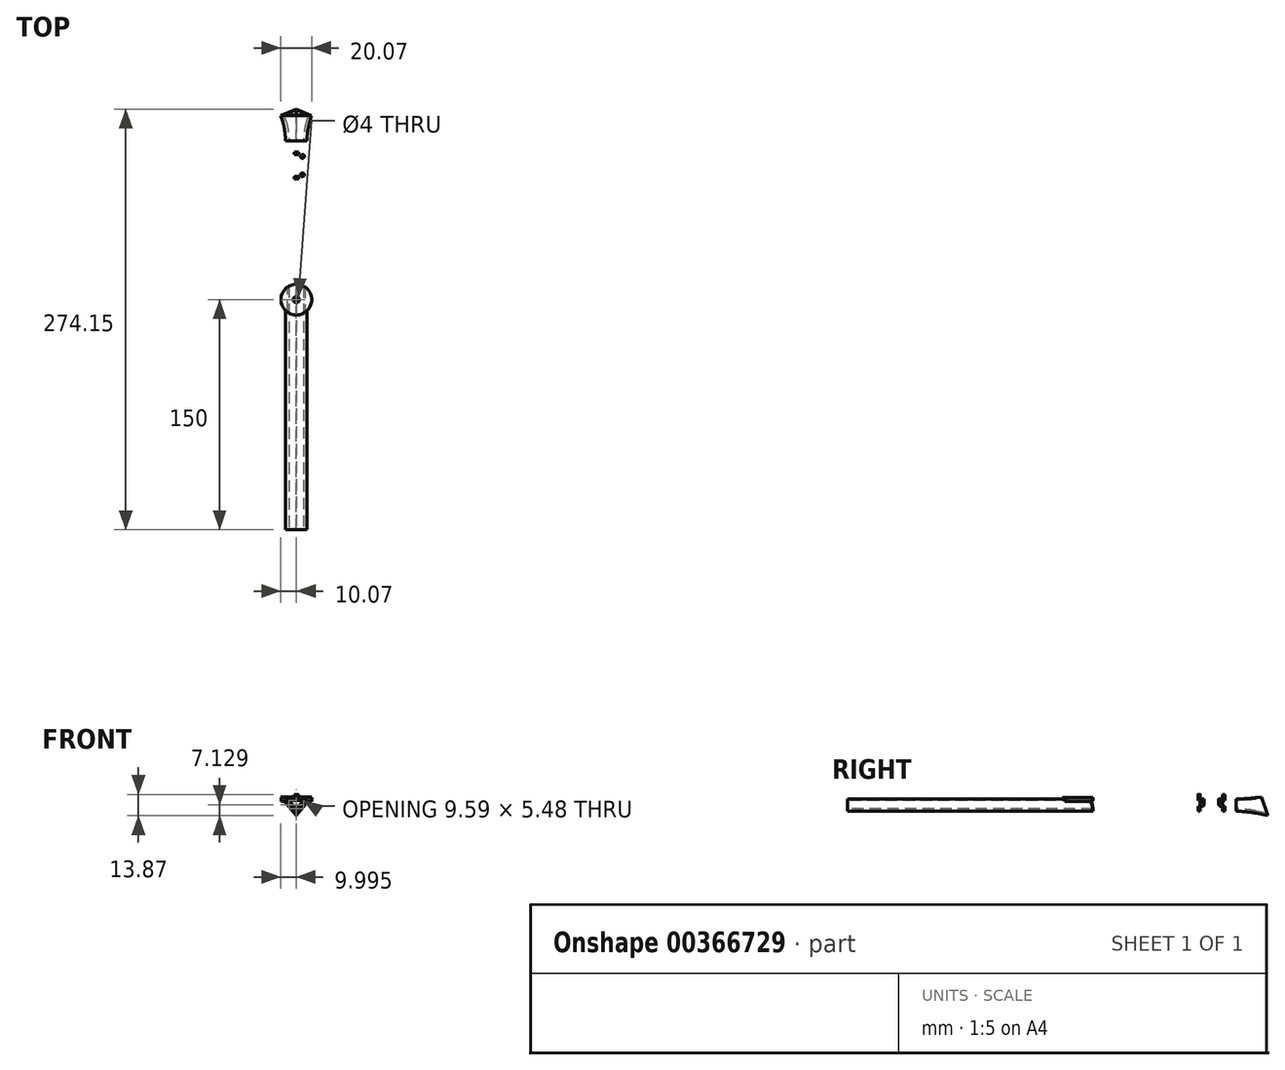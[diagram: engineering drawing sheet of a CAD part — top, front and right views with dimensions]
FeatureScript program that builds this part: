
annotation { "Feature Type Name" : "Feature", "Feature Type Description" : "" }
export const myFeature = defineFeature(function(context is Context, id is Id, definition is map)
    precondition{}
    {
        {
            var Q0;
            Q0=qCreatedBy(makeId("Front.planeOp"),FACE);
            var sketch = newSketch(context, id + "F0", { "sketchPlane" : qUnion([Q0])});
            skLineSegment(sketch, "E0", {"start": v(-7.1, 0) * mm, "end": v(6.9, 0) * mm});
            skLineSegment(sketch, "E1", {"start": v(6.9, 0) * mm, "end": v(0, -8) * mm});
            skLineSegment(sketch, "E2", {"start": v(0, -8) * mm, "end": v(-7.1, 0) * mm});
            skSolve(sketch);
        }
        {
            var Q0;
            Q0=makeQuery(id+"F0.imprint","IMPRINT",FACE,{"disambiguationData":[TD([[makeQuery(id+"F0.imprint","IMPRINT",EDGE,{"derivedFrom":sQuery(id+"F0.wireOp",EDGE,"E0")}),-1.0]])]});
            extrude(context, id + "F1", {"entities" : qUnion([Q0]), "depth" : 150 * mm});
        }
        {
            var Q0;
            Q0=makeQuery(id+"F1.opExtrude","CAP_FACE",FACE,{"disambiguationData":[OSD([sQuery(id+"F0.wireOp",EDGE,"E0"),sQuery(id+"F0.wireOp",EDGE,"E1"),sQuery(id+"F0.wireOp",EDGE,"E2")])],"isStart":true});
            extrude(context, id + "F2", {"entities" : qUnion([Q0]), "operationType" : NewBodyOperationType.ADD, "depth" : 110 * mm});
        }
        {
            var Q0;
            {var subQ0=sQuery(id+"F0.wireOp",EDGE,"E0");Q0=makeQuery(id+"F2.boolean.opBoolean","MERGE",FACE,{"derivedFrom":[makeQuery(id+"F1.opExtrude","SWEPT_FACE",FACE,{"disambiguationData":[OSD([subQ0])]}),makeQuery(id+"F2.opExtrude","SWEPT_FACE",FACE,{"disambiguationData":[OSD([subQ0])]})]});}
            var sketch = newSketch(context, id + "F3", { "sketchPlane" : qUnion([Q0])});
            skCircle(sketch, "E3", {"center": v(0, 0) * mm, "radius": 10 * mm});
            skCircle(sketch, "E4", {"center": v(0, 0) * mm, "radius": 2 * mm});
            skSolve(sketch);
        }
        {
            var Q0;
            {var subQ0=sQuery(id+"F3.wireOp",EDGE,"E3");var subQ1=sQuery(id+"F0.wireOp",EDGE,"E2");var subQ2=sQuery(id+"F0.wireOp",EDGE,"E0");var subQ3=makeQuery(id+"F2.boolean.opBoolean","MERGE",EDGE,{"derivedFrom":[makeQuery(id+"F1.opExtrude","SWEPT_EDGE",EDGE,{"disambiguationData":[OSD([subQ2,subQ1])]}),makeQuery(id+"F2.opExtrude","SWEPT_EDGE",EDGE,{"disambiguationData":[OSD([subQ2,subQ1])]})]});var subQ4=makeQuery(id+"F3.imprint","INTERSECT",VERTEX,{"disambiguationData":[OD(0.0)],"derivedFrom":[subQ3,subQ0]});Q0=makeQuery(id+"F3.imprint","IMPRINT",FACE,{"disambiguationData":[TD([[makeQuery(id+"F3.imprint","IMPRINT",EDGE,{"disambiguationData":[TD([[subQ4,1.0]])],"derivedFrom":subQ0}),1.0]])]});}
            var Q1;
            {var subQ0=sQuery(id+"F3.wireOp",EDGE,"E3");var subQ1=sQuery(id+"F0.wireOp",EDGE,"E2");var subQ2=sQuery(id+"F0.wireOp",EDGE,"E0");var subQ3=makeQuery(id+"F2.boolean.opBoolean","MERGE",EDGE,{"derivedFrom":[makeQuery(id+"F1.opExtrude","SWEPT_EDGE",EDGE,{"disambiguationData":[OSD([subQ2,subQ1])]}),makeQuery(id+"F2.opExtrude","SWEPT_EDGE",EDGE,{"disambiguationData":[OSD([subQ2,subQ1])]})]});var subQ4=makeQuery(id+"F3.imprint","INTERSECT",VERTEX,{"disambiguationData":[OD(0.0)],"derivedFrom":[subQ3,subQ0]});Q1=makeQuery(id+"F3.imprint","IMPRINT",FACE,{"disambiguationData":[TD([[makeQuery(id+"F3.imprint","IMPRINT",EDGE,{"disambiguationData":[TD([[subQ4,-1.0]])],"derivedFrom":subQ0}),1.0]])]});}
            var Q2;
            {var subQ0=sQuery(id+"F3.wireOp",EDGE,"E3");var subQ1=sQuery(id+"F0.wireOp",EDGE,"E1");var subQ2=sQuery(id+"F0.wireOp",EDGE,"E0");var subQ3=makeQuery(id+"F2.boolean.opBoolean","MERGE",EDGE,{"derivedFrom":[makeQuery(id+"F1.opExtrude","SWEPT_EDGE",EDGE,{"disambiguationData":[OSD([subQ2,subQ1])]}),makeQuery(id+"F2.opExtrude","SWEPT_EDGE",EDGE,{"disambiguationData":[OSD([subQ2,subQ1])]})]});var subQ4=makeQuery(id+"F3.imprint","INTERSECT",VERTEX,{"disambiguationData":[OD(0.0)],"derivedFrom":[subQ3,subQ0]});Q2=makeQuery(id+"F3.imprint","IMPRINT",FACE,{"disambiguationData":[TD([[makeQuery(id+"F3.imprint","IMPRINT",EDGE,{"disambiguationData":[TD([[subQ4,1.0]])],"derivedFrom":subQ0}),1.0]])]});}
            extrude(context, id + "F4", {"entities" : qUnion([Q0, Q1, Q2]), "operationType" : NewBodyOperationType.ADD, "oppositeDirection" : true, "depth" : 1.5 * mm});
        }
        {
            var Q0;
            Q0 = qSketchRegion(id + "F3", true);
            extrude(context, id + "F5", {"entities" : qUnion([Q0]), "operationType" : NewBodyOperationType.ADD, "depth" : 1 * mm});
        }
        {
            var Q0;
            Q0=makeQuery(id+"F1.opExtrude","CAP_FACE",FACE,{"disambiguationData":[OSD([sQuery(id+"F0.wireOp",EDGE,"E0"),sQuery(id+"F0.wireOp",EDGE,"E1"),sQuery(id+"F0.wireOp",EDGE,"E2")])],"isStart":false});
            var sketch = newSketch(context, id + "F6", { "sketchPlane" : qUnion([Q0])});
            skLineSegment(sketch, "E5.0", {"start": v(-4.87, -1) * mm, "end": v(-0.01, -6.48) * mm});
            skLineSegment(sketch, "E5.1", {"start": v(4.72, -1) * mm, "end": v(-4.87, -1) * mm});
            skLineSegment(sketch, "E5.2", {"start": v(-0.01, -6.48) * mm, "end": v(4.72, -1) * mm});
            skSolve(sketch);
        }
        {
            var Q0;
            Q0=makeQuery(id+"F6.imprint","IMPRINT",FACE,{"disambiguationData":[TD([[makeQuery(id+"F6.imprint","IMPRINT",EDGE,{"derivedFrom":sQuery(id+"F6.wireOp",EDGE,"E5.0")}),1.0]])]});
            extrude(context, id + "F7", {"entities" : qUnion([Q0]), "operationType" : NewBodyOperationType.REMOVE, "endBound" : BoundingType.THROUGH_ALL, "oppositeDirection" : true, "depth" : 25 * mm});
        }
        {
            var Q0;
            {var subQ0=sQuery(id+"F3.wireOp",EDGE,"E4");var subQ1=sQuery(id+"F0.wireOp",EDGE,"E0");Q0=makeQuery(id+"F5.boolean.opBoolean","SPLIT",FACE,{"disambiguationData":[TD([makeQuery(id+"F5.opExtrude","SWEPT_FACE",FACE,{"disambiguationData":[OSD([subQ0])]})])],"derivedFrom":makeQuery(id+"F4.boolean.opBoolean","MERGE",FACE,{"derivedFrom":[makeQuery(id+"F2.boolean.opBoolean","MERGE",FACE,{"derivedFrom":[makeQuery(id+"F1.opExtrude","SWEPT_FACE",FACE,{"disambiguationData":[OSD([subQ1])]}),makeQuery(id+"F2.opExtrude","SWEPT_FACE",FACE,{"disambiguationData":[OSD([subQ1])]})]}),makeQuery(id+"F4.opExtrude","CAP_FACE",FACE,{"disambiguationData":[OSD([sQuery(id+"F3.wireOp",EDGE,"E3"),subQ0])],"isStart":true})]})});}
            extrude(context, id + "F8", {"entities" : qUnion([Q0]), "operationType" : NewBodyOperationType.REMOVE, "oppositeDirection" : true, "depth" : 1 * mm});
        }
        {
            var Q0;
            Q0=makeQuery(id+"F2.opExtrude","CAP_FACE",FACE,{"disambiguationData":[OSD([sQuery(id+"F0.wireOp",EDGE,"E0"),sQuery(id+"F0.wireOp",EDGE,"E1"),sQuery(id+"F0.wireOp",EDGE,"E2")])],"isStart":false});
            var sketch = newSketch(context, id + "F9", { "sketchPlane" : qUnion([Q0])});
            skLineSegment(sketch, "E6.0.0", {"start": v(0, -8) * mm, "end": v(7.1, 0) * mm});
            skLineSegment(sketch, "E6.0.1", {"start": v(7.1, 0) * mm, "end": v(-6.9, 0) * mm});
            skLineSegment(sketch, "E6.0.2", {"start": v(-6.9, 0) * mm, "end": v(0, -8) * mm});
            skLineSegment(sketch, "E7.0", {"start": v(-0.02, -11.04) * mm, "end": v(11.54, 2) * mm});
            skLineSegment(sketch, "E7.1", {"start": v(-11.27, 2) * mm, "end": v(-0.02, -11.04) * mm});
            skLineSegment(sketch, "E7.2", {"start": v(11.54, 2) * mm, "end": v(-11.27, 2) * mm});
            skSolve(sketch);
        }
        {
            var Q0;
            Q0=makeQuery(id+"F9.imprint","IMPRINT",FACE,{"disambiguationData":[TD([[makeQuery(id+"F9.imprint","IMPRINT",EDGE,{"derivedFrom":sQuery(id+"F9.wireOp",EDGE,"E6.0.0")}),1.0]])]});
            var Q1;
            Q1=makeQuery(id+"F9.imprint","IMPRINT",FACE,{"disambiguationData":[TD([[makeQuery(id+"F9.imprint","IMPRINT",EDGE,{"derivedFrom":sQuery(id+"F9.wireOp",EDGE,"E6.0.0")}),-1.0]])]});
            extrude(context, id + "F10", {"entities" : qUnion([Q0, Q1]), "operationType" : NewBodyOperationType.ADD, "depth" : 15 * mm});
        }
        {
            var Q0;
            Q0=makeQuery(id+"F10.opExtrude","CAP_EDGE",EDGE,{"disambiguationData":[OSD([sQuery(id+"F0.wireOp",EDGE,"E0"),sQuery(id+"F0.wireOp",EDGE,"E1"),sQuery(id+"F0.wireOp",EDGE,"E2"),sQuery(id+"F6.wireOp",EDGE,"E5.1")])],"isStart":false});
            var Q1;
            Q1=makeQuery(id+"F10.opExtrude","CAP_EDGE",EDGE,{"disambiguationData":[OSD([sQuery(id+"F0.wireOp",EDGE,"E0"),sQuery(id+"F0.wireOp",EDGE,"E1"),sQuery(id+"F0.wireOp",EDGE,"E2"),sQuery(id+"F6.wireOp",EDGE,"E5.2")])],"isStart":false});
            var Q2;
            Q2=makeQuery(id+"F10.opExtrude","CAP_EDGE",EDGE,{"disambiguationData":[OSD([sQuery(id+"F0.wireOp",EDGE,"E0"),sQuery(id+"F0.wireOp",EDGE,"E1"),sQuery(id+"F0.wireOp",EDGE,"E2"),sQuery(id+"F6.wireOp",EDGE,"E5.0")])],"isStart":false});
            chamfer(context, id + "F11", {"entities" : qUnion([Q0, Q1, Q2]), "chamferType" : ChamferType.TWO_OFFSETS, "width1" : 2 * mm, "oppositeDirection" : false, "width2" : 15 * mm, "tangentPropagation" : true});
        }
        {
            var Q0;
            Q0=makeQuery(id+"F10.opExtrude","CAP_EDGE",EDGE,{"disambiguationData":[OSD([sQuery(id+"F9.wireOp",EDGE,"E7.2")])],"isStart":true});
            var Q1;
            Q1=makeQuery(id+"F10.opExtrude","CAP_EDGE",EDGE,{"disambiguationData":[OSD([sQuery(id+"F9.wireOp",EDGE,"E7.1")])],"isStart":true});
            var Q2;
            Q2=makeQuery(id+"F10.opExtrude","CAP_EDGE",EDGE,{"disambiguationData":[OSD([sQuery(id+"F9.wireOp",EDGE,"E7.0")])],"isStart":true});
            chamfer(context, id + "F12", {"entities" : qUnion([Q0, Q1, Q2]), "chamferType" : ChamferType.TWO_OFFSETS, "width1" : 15 * mm, "oppositeDirection" : false, "width2" : 2 * mm, "tangentPropagation" : true});
        }
        {
            var Q0;
            Q0=makeQuery(id+"F12.opChamfer","BLEND_FACE",FACE,{"disambiguationData":[OSD([sQuery(id+"F9.wireOp",EDGE,"E7.2")])]});
            var sketch = newSketch(context, id + "F13", { "sketchPlane" : qUnion([Q0])});
            skLineSegment(sketch, "E8.0.1", {"start": v(11.27, 124.17) * mm, "end": v(-11.54, 124.17) * mm});
            skLineSegment(sketch, "E9", {"start": v(-0.13, 124.17) * mm, "end": v(-0.13, 119.17) * mm, "construction": true});
            skPoint(sketch, "E10", {"position": v(-10.07, 119.17) * mm});
            skLineSegment(sketch, "E11", {"start": v(-10.07, 119.17) * mm, "end": v(9.83, 119.17) * mm});
            skLineSegment(sketch, "E12", {"start": v(-11.54, 124.17) * mm, "end": v(-10.07, 119.17) * mm});
            skLineSegment(sketch, "E13", {"start": v(11.27, 124.17) * mm, "end": v(9.83, 119.17) * mm});
            skSolve(sketch);
        }
        {
            var Q0;
            Q0=makeQuery(id+"F13.imprint","IMPRINT",FACE,{"disambiguationData":[TD([[makeQuery(id+"F13.imprint","IMPRINT",EDGE,{"derivedFrom":sQuery(id+"F13.wireOp",EDGE,"E8.0.1")}),-1.0]])]});
            var Q1;
            Q1=sQuery(id+"F13.wireOp",EDGE,"E11");
            revolve(context, id + "F14", {"operationType" : NewBodyOperationType.ADD, "entities" : qUnion([Q0]), "axis" : qUnion([Q1]), "revolveType" : RevolveType.ONE_DIRECTION, "angle" : 11 * degree});
        }
        {
            var Q0;
            Q0=makeQuery(id+"F14.opRevolve","CAP_FACE",FACE,{"disambiguationData":[OSD([sQuery(id+"F13.wireOp",EDGE,"E8.0.1"),sQuery(id+"F13.wireOp",EDGE,"E11"),sQuery(id+"F13.wireOp",EDGE,"E12"),sQuery(id+"F13.wireOp",EDGE,"E13")])],"isStart":false});
            var sketch = newSketch(context, id + "F15", { "sketchPlane" : qUnion([Q0])});
            skLineSegment(sketch, "E14.bottom", {"start": v(-32.64, 114.2) * mm, "end": v(17.36, 114.2) * mm});
            skLineSegment(sketch, "E14.top", {"start": v(-32.64, 126.44) * mm, "end": v(17.36, 126.44) * mm});
            skLineSegment(sketch, "E14.left", {"start": v(-32.64, 114.2) * mm, "end": v(-32.64, 126.44) * mm});
            skLineSegment(sketch, "E14.right", {"start": v(17.36, 114.2) * mm, "end": v(17.36, 126.44) * mm});
            skSolve(sketch);
        }
        {
            var Q0;
            Q0=makeQuery(id+"F15.imprint","IMPRINT",FACE,{"disambiguationData":[TD([[makeQuery(id+"F15.imprint","IMPRINT",EDGE,{"derivedFrom":sQuery(id+"F15.wireOp",EDGE,"E14.top")}),-1.0]])]});
            var Q1;
            Q1=makeQuery(id+"F15.imprint","IMPRINT",FACE,{"disambiguationData":[TD([[makeQuery(id+"F15.imprint","IMPRINT",EDGE,{"derivedFrom":makeQuery(id+"F14.opRevolve","CAP_EDGE",EDGE,{"disambiguationData":[OSD([sQuery(id+"F13.wireOp",EDGE,"E8.0.1")])],"isStart":false})}),-1.0]])]});
            extrude(context, id + "F16", {"entities" : qUnion([Q0, Q1]), "operationType" : NewBodyOperationType.REMOVE, "endBound" : BoundingType.THROUGH_ALL, "oppositeDirection" : true, "depth" : 25 * mm});
        }
        {
            var Q0;
            {var subQ0=sQuery(id+"F0.wireOp",EDGE,"E1");var subQ1=sQuery(id+"F0.wireOp",EDGE,"E2");var subQ2=sQuery(id+"F3.wireOp",EDGE,"E3");var subQ3=sQuery(id+"F0.wireOp",EDGE,"E0");Q0=makeQuery(id+"F12.opChamfer","BLEND_EDGE",EDGE,{"blendedFrom":[makeQuery(id+"F10.opExtrude","CAP_EDGE",EDGE,{"disambiguationData":[OSD([sQuery(id+"F9.wireOp",EDGE,"E7.2")])],"isStart":true}),makeQuery(id+"F5.boolean.opBoolean","SPLIT",FACE,{"disambiguationData":[TD([makeQuery(id+"F2.opExtrude","CAP_FACE",FACE,{"disambiguationData":[OSD([subQ3,subQ0,subQ1])],"isStart":false})])],"derivedFrom":makeQuery(id+"F4.boolean.opBoolean","MERGE",FACE,{"derivedFrom":[makeQuery(id+"F2.boolean.opBoolean","MERGE",FACE,{"derivedFrom":[makeQuery(id+"F1.opExtrude","SWEPT_FACE",FACE,{"disambiguationData":[OSD([subQ3])]}),makeQuery(id+"F2.opExtrude","SWEPT_FACE",FACE,{"disambiguationData":[OSD([subQ3])]})]}),makeQuery(id+"F4.opExtrude","CAP_FACE",FACE,{"disambiguationData":[OSD([subQ2,sQuery(id+"F3.wireOp",EDGE,"E4")])],"isStart":true})]})})],"blendedInto":[makeQuery(id+"F5.boolean.opBoolean","SPLIT",FACE,{"disambiguationData":[TD([makeQuery(id+"F2.opExtrude","CAP_FACE",FACE,{"disambiguationData":[OSD([subQ3,subQ0,subQ1])],"isStart":false})])],"derivedFrom":makeQuery(id+"F4.boolean.opBoolean","MERGE",FACE,{"derivedFrom":[makeQuery(id+"F2.boolean.opBoolean","MERGE",FACE,{"derivedFrom":[makeQuery(id+"F1.opExtrude","SWEPT_FACE",FACE,{"disambiguationData":[OSD([subQ3])]}),makeQuery(id+"F2.opExtrude","SWEPT_FACE",FACE,{"disambiguationData":[OSD([subQ3])]})]}),makeQuery(id+"F4.opExtrude","CAP_FACE",FACE,{"disambiguationData":[OSD([subQ2,sQuery(id+"F3.wireOp",EDGE,"E4")])],"isStart":true})]})})]});}
            var Q1;
            {var subQ0=sQuery(id+"F0.wireOp",EDGE,"E2");Q1=makeQuery(id+"F12.opChamfer","BLEND_EDGE",EDGE,{"blendedFrom":[makeQuery(id+"F10.opExtrude","CAP_EDGE",EDGE,{"disambiguationData":[OSD([sQuery(id+"F9.wireOp",EDGE,"E7.0")])],"isStart":true}),makeQuery(id+"F2.boolean.opBoolean","MERGE",FACE,{"derivedFrom":[makeQuery(id+"F1.opExtrude","SWEPT_FACE",FACE,{"disambiguationData":[OSD([subQ0])]}),makeQuery(id+"F2.opExtrude","SWEPT_FACE",FACE,{"disambiguationData":[OSD([subQ0])]})]})],"blendedInto":[makeQuery(id+"F2.boolean.opBoolean","MERGE",FACE,{"derivedFrom":[makeQuery(id+"F1.opExtrude","SWEPT_FACE",FACE,{"disambiguationData":[OSD([subQ0])]}),makeQuery(id+"F2.opExtrude","SWEPT_FACE",FACE,{"disambiguationData":[OSD([subQ0])]})]})]});}
            var Q2;
            {var subQ0=sQuery(id+"F0.wireOp",EDGE,"E1");Q2=makeQuery(id+"F12.opChamfer","BLEND_EDGE",EDGE,{"blendedFrom":[makeQuery(id+"F10.opExtrude","CAP_EDGE",EDGE,{"disambiguationData":[OSD([sQuery(id+"F9.wireOp",EDGE,"E7.1")])],"isStart":true}),makeQuery(id+"F2.boolean.opBoolean","MERGE",FACE,{"derivedFrom":[makeQuery(id+"F1.opExtrude","SWEPT_FACE",FACE,{"disambiguationData":[OSD([subQ0])]}),makeQuery(id+"F2.opExtrude","SWEPT_FACE",FACE,{"disambiguationData":[OSD([subQ0])]})]})],"blendedInto":[makeQuery(id+"F2.boolean.opBoolean","MERGE",FACE,{"derivedFrom":[makeQuery(id+"F1.opExtrude","SWEPT_FACE",FACE,{"disambiguationData":[OSD([subQ0])]}),makeQuery(id+"F2.opExtrude","SWEPT_FACE",FACE,{"disambiguationData":[OSD([subQ0])]})]})]});}
            var Q3;
            {var subQ0=sQuery(id+"F6.wireOp",EDGE,"E5.2");var subQ1=sQuery(id+"F0.wireOp",EDGE,"E2");var subQ2=sQuery(id+"F0.wireOp",EDGE,"E1");var subQ3=sQuery(id+"F0.wireOp",EDGE,"E0");Q3=makeQuery(id+"F11.opChamfer","BLEND_EDGE",EDGE,{"blendedFrom":[makeQuery(id+"F10.opExtrude","CAP_EDGE",EDGE,{"disambiguationData":[OSD([subQ3,subQ2,subQ1,subQ0])],"isStart":false}),makeQuery(id+"F10.boolean.opBoolean","MERGE",FACE,{"derivedFrom":[makeQuery(id+"F7.boolean.opBoolean","COPY",FACE,{"derivedFrom":makeQuery(id+"F7.opExtrude","SWEPT_FACE",FACE,{"disambiguationData":[OSD([subQ0])]})}),makeQuery(id+"F10.opExtrude","SWEPT_FACE",FACE,{"disambiguationData":[OSD([subQ3,subQ2,subQ1,subQ0])]})]})],"blendedInto":[makeQuery(id+"F10.boolean.opBoolean","MERGE",FACE,{"derivedFrom":[makeQuery(id+"F7.boolean.opBoolean","COPY",FACE,{"derivedFrom":makeQuery(id+"F7.opExtrude","SWEPT_FACE",FACE,{"disambiguationData":[OSD([subQ0])]})}),makeQuery(id+"F10.opExtrude","SWEPT_FACE",FACE,{"disambiguationData":[OSD([subQ3,subQ2,subQ1,subQ0])]})]})]});}
            var Q4;
            {var subQ0=sQuery(id+"F6.wireOp",EDGE,"E5.1");var subQ1=sQuery(id+"F0.wireOp",EDGE,"E2");var subQ2=sQuery(id+"F0.wireOp",EDGE,"E1");var subQ3=sQuery(id+"F0.wireOp",EDGE,"E0");Q4=makeQuery(id+"F11.opChamfer","BLEND_EDGE",EDGE,{"blendedFrom":[makeQuery(id+"F10.opExtrude","CAP_EDGE",EDGE,{"disambiguationData":[OSD([subQ3,subQ2,subQ1,subQ0])],"isStart":false}),makeQuery(id+"F10.boolean.opBoolean","MERGE",FACE,{"derivedFrom":[makeQuery(id+"F7.boolean.opBoolean","COPY",FACE,{"derivedFrom":makeQuery(id+"F7.opExtrude","SWEPT_FACE",FACE,{"disambiguationData":[OSD([subQ0])]})}),makeQuery(id+"F10.opExtrude","SWEPT_FACE",FACE,{"disambiguationData":[OSD([subQ3,subQ2,subQ1,subQ0])]})]})],"blendedInto":[makeQuery(id+"F10.boolean.opBoolean","MERGE",FACE,{"derivedFrom":[makeQuery(id+"F7.boolean.opBoolean","COPY",FACE,{"derivedFrom":makeQuery(id+"F7.opExtrude","SWEPT_FACE",FACE,{"disambiguationData":[OSD([subQ0])]})}),makeQuery(id+"F10.opExtrude","SWEPT_FACE",FACE,{"disambiguationData":[OSD([subQ3,subQ2,subQ1,subQ0])]})]})]});}
            var Q5;
            {var subQ0=sQuery(id+"F6.wireOp",EDGE,"E5.0");var subQ1=sQuery(id+"F0.wireOp",EDGE,"E2");var subQ2=sQuery(id+"F0.wireOp",EDGE,"E1");var subQ3=sQuery(id+"F0.wireOp",EDGE,"E0");Q5=makeQuery(id+"F11.opChamfer","BLEND_EDGE",EDGE,{"blendedFrom":[makeQuery(id+"F10.opExtrude","CAP_EDGE",EDGE,{"disambiguationData":[OSD([subQ3,subQ2,subQ1,subQ0])],"isStart":false}),makeQuery(id+"F10.boolean.opBoolean","MERGE",FACE,{"derivedFrom":[makeQuery(id+"F7.boolean.opBoolean","COPY",FACE,{"derivedFrom":makeQuery(id+"F7.opExtrude","SWEPT_FACE",FACE,{"disambiguationData":[OSD([subQ0])]})}),makeQuery(id+"F10.opExtrude","SWEPT_FACE",FACE,{"disambiguationData":[OSD([subQ3,subQ2,subQ1,subQ0])]})]})],"blendedInto":[makeQuery(id+"F10.boolean.opBoolean","MERGE",FACE,{"derivedFrom":[makeQuery(id+"F7.boolean.opBoolean","COPY",FACE,{"derivedFrom":makeQuery(id+"F7.opExtrude","SWEPT_FACE",FACE,{"disambiguationData":[OSD([subQ0])]})}),makeQuery(id+"F10.opExtrude","SWEPT_FACE",FACE,{"disambiguationData":[OSD([subQ3,subQ2,subQ1,subQ0])]})]})]});}
            fillet(context, id + "F17", {"entities" : qUnion([Q0, Q1, Q2, Q3, Q4, Q5]), "radius" : 100 * mm, "tangentPropagation" : true, "allowEdgeOverflow" : false});
        }
        {
            var Q0;
            {var subQ0=sQuery(id+"F0.wireOp",EDGE,"E1");var subQ1=sQuery(id+"F0.wireOp",EDGE,"E2");var subQ2=sQuery(id+"F3.wireOp",EDGE,"E3");var subQ3=sQuery(id+"F0.wireOp",EDGE,"E0");Q0=makeQuery(id+"F5.boolean.opBoolean","SPLIT",FACE,{"disambiguationData":[TD([makeQuery(id+"F2.opExtrude","CAP_FACE",FACE,{"disambiguationData":[OSD([subQ3,subQ0,subQ1])],"isStart":false})])],"derivedFrom":makeQuery(id+"F4.boolean.opBoolean","MERGE",FACE,{"derivedFrom":[makeQuery(id+"F2.boolean.opBoolean","MERGE",FACE,{"derivedFrom":[makeQuery(id+"F1.opExtrude","SWEPT_FACE",FACE,{"disambiguationData":[OSD([subQ3])]}),makeQuery(id+"F2.opExtrude","SWEPT_FACE",FACE,{"disambiguationData":[OSD([subQ3])]})]}),makeQuery(id+"F4.opExtrude","CAP_FACE",FACE,{"disambiguationData":[OSD([subQ2,sQuery(id+"F3.wireOp",EDGE,"E4")])],"isStart":true})]})});}
            var sketch = newSketch(context, id + "F18", { "sketchPlane" : qUnion([Q0])});
            skLineSegment(sketch, "E15", {"start": v(0, 103.36) * mm, "end": v(0, 93.36) * mm, "construction": true});
            skLineSegment(sketch, "E16", {"start": v(0, 93.36) * mm, "end": v(0, 81.36) * mm, "construction": true});
            skLineSegment(sketch, "E17", {"start": v(0, 93.36) * mm, "end": v(-4, 93.36) * mm, "construction": true});
            skLineSegment(sketch, "E18", {"start": v(0, 81.36) * mm, "end": v(-4, 81.36) * mm, "construction": true});
            skCircle(sketch, "E19", {"center": v(-4, 81.36) * mm, "radius": 1.25 * mm});
            skCircle(sketch, "E20", {"center": v(-4, 93.36) * mm, "radius": 1.25 * mm});
            skCircle(sketch, "E21.MirrorC", {"center": v(4, 93.36) * mm, "radius": 1.25 * mm});
            skCircle(sketch, "E22.MirrorC", {"center": v(4, 81.36) * mm, "radius": 1.25 * mm});
            skLineSegment(sketch, "E23", {"start": v(0, 103.36) * mm, "end": v(0, 95.36) * mm, "construction": true});
            skLineSegment(sketch, "E24.bottom", {"start": v(1.5, 96.11) * mm, "end": v(-1.5, 96.11) * mm});
            skLineSegment(sketch, "E24.top", {"start": v(1.5, 94.61) * mm, "end": v(-1.5, 94.61) * mm});
            skLineSegment(sketch, "E24.left", {"start": v(1.5, 96.11) * mm, "end": v(1.5, 94.61) * mm});
            skLineSegment(sketch, "E24.right", {"start": v(-1.5, 96.11) * mm, "end": v(-1.5, 94.61) * mm});
            skPoint(sketch, "E24.middle", {"position": v(0, 95.36) * mm});
            skLineSegment(sketch, "E25.MirrorCS", {"start": v(1.5, 80.11) * mm, "end": v(-1.5, 80.11) * mm});
            skLineSegment(sketch, "E26.MirrorCS", {"start": v(1.5, 78.61) * mm, "end": v(1.5, 80.11) * mm});
            skLineSegment(sketch, "E27.MirrorCS", {"start": v(1.5, 78.61) * mm, "end": v(-1.5, 78.61) * mm});
            skLineSegment(sketch, "E28.MirrorCS", {"start": v(-1.5, 78.61) * mm, "end": v(-1.5, 80.11) * mm});
            skSolve(sketch);
        }
        {
            var Q0;
            Q0=makeQuery(id+"F18.imprint","IMPRINT",FACE,{"disambiguationData":[TD([[makeQuery(id+"F18.imprint","IMPRINT",EDGE,{"derivedFrom":sQuery(id+"F18.wireOp",EDGE,"E20")}),1.0]])]});
            var Q1;
            Q1=makeQuery(id+"F18.imprint","IMPRINT",FACE,{"disambiguationData":[TD([[makeQuery(id+"F18.imprint","IMPRINT",EDGE,{"derivedFrom":sQuery(id+"F18.wireOp",EDGE,"E19")}),1.0]])]});
            var Q2;
            Q2=makeQuery(id+"F18.imprint","IMPRINT",FACE,{"disambiguationData":[TD([[makeQuery(id+"F18.imprint","IMPRINT",EDGE,{"derivedFrom":sQuery(id+"F18.wireOp",EDGE,"E21.MirrorC")}),-1.0]])]});
            var Q3;
            Q3=makeQuery(id+"F18.imprint","IMPRINT",FACE,{"disambiguationData":[TD([[makeQuery(id+"F18.imprint","IMPRINT",EDGE,{"derivedFrom":sQuery(id+"F18.wireOp",EDGE,"E22.MirrorC")}),-1.0]])]});
            extrude(context, id + "F19", {"entities" : qUnion([Q0, Q1, Q2, Q3]), "operationType" : NewBodyOperationType.REMOVE, "endBound" : BoundingType.THROUGH_ALL, "oppositeDirection" : true, "depth" : 25 * mm});
        }
        {
            var Q0;
            Q0=makeQuery(id+"F18.imprint","IMPRINT",FACE,{"disambiguationData":[TD([[makeQuery(id+"F18.imprint","IMPRINT",EDGE,{"derivedFrom":sQuery(id+"F18.wireOp",EDGE,"E25.MirrorCS")}),1.0]])]});
            var Q1;
            Q1=makeQuery(id+"F18.imprint","IMPRINT",FACE,{"disambiguationData":[TD([[makeQuery(id+"F18.imprint","IMPRINT",EDGE,{"derivedFrom":sQuery(id+"F18.wireOp",EDGE,"E24.bottom")}),1.0]])]});
            extrude(context, id + "F20", {"entities" : qUnion([Q0, Q1]), "operationType" : NewBodyOperationType.ADD, "depth" : 3 * mm});
        }
        {
            var Q0;
            Q0=makeQuery(id+"F20.opExtrude","SWEPT_FACE",FACE,{"disambiguationData":[OSD([sQuery(id+"F18.wireOp",EDGE,"E24.bottom")])]});
            var sketch = newSketch(context, id + "F21", { "sketchPlane" : qUnion([Q0])});
            skLineSegment(sketch, "E29", {"start": v(1.5, 3) * mm, "end": v(1.5, 2) * mm, "construction": true});
            skLineSegment(sketch, "E30.bottom", {"start": v(1.5, 2) * mm, "end": v(0, 2) * mm});
            skLineSegment(sketch, "E30.top", {"start": v(1.5, 1) * mm, "end": v(0, 1) * mm});
            skLineSegment(sketch, "E30.left", {"start": v(1.5, 2) * mm, "end": v(1.5, 1) * mm});
            skLineSegment(sketch, "E30.right", {"start": v(0, 2) * mm, "end": v(0, 1) * mm});
            skSolve(sketch);
        }
        {
            var Q0;
            Q0 = qSketchRegion(id + "F21", true);
            extrude(context, id + "F22", {"entities" : qUnion([Q0]), "operationType" : NewBodyOperationType.REMOVE, "oppositeDirection" : true, "depth" : 2 * mm});
        }
        {
            var Q0;
            Q0=makeQuery(id+"F20.opExtrude","CAP_EDGE",EDGE,{"disambiguationData":[OSD([sQuery(id+"F18.wireOp",EDGE,"E24.right")])],"isStart":false});
            chamfer(context, id + "F23", {"entities" : qUnion([Q0]), "width" : 0.8 * mm, "tangentPropagation" : true});
        }
        {
            var Q0;
            {var subQ0=sQuery(id+"F18.wireOp",EDGE,"E24.right");Q0=makeQuery(id+"F23.opChamfer","BLEND_EDGE",EDGE,{"blendedFrom":[makeQuery(id+"F20.opExtrude","CAP_EDGE",EDGE,{"disambiguationData":[OSD([subQ0])],"isStart":false}),makeQuery(id+"F20.opExtrude","CAP_FACE",FACE,{"disambiguationData":[OSD([sQuery(id+"F18.wireOp",EDGE,"E24.bottom"),sQuery(id+"F18.wireOp",EDGE,"E24.top"),sQuery(id+"F18.wireOp",EDGE,"E24.left"),subQ0])],"isStart":false})],"blendedInto":[makeQuery(id+"F20.opExtrude","CAP_FACE",FACE,{"disambiguationData":[OSD([sQuery(id+"F18.wireOp",EDGE,"E24.bottom"),sQuery(id+"F18.wireOp",EDGE,"E24.top"),sQuery(id+"F18.wireOp",EDGE,"E24.left"),subQ0])],"isStart":false})]});}
            fillet(context, id + "F24", {"entities" : qUnion([Q0]), "radius" : 1 * mm, "tangentPropagation" : true, "allowEdgeOverflow" : false});
        }
        {
            var Q0;
            Q0=makeQuery(id+"F20.opExtrude","SWEPT_FACE",FACE,{"disambiguationData":[OSD([sQuery(id+"F18.wireOp",EDGE,"E27.MirrorCS")])]});
            var sketch = newSketch(context, id + "F25", { "sketchPlane" : qUnion([Q0])});
            skLineSegment(sketch, "E31", {"start": v(1.5, 3) * mm, "end": v(1.5, 2) * mm, "construction": true});
            skLineSegment(sketch, "E32.bottom", {"start": v(1.5, 2) * mm, "end": v(0, 2) * mm});
            skLineSegment(sketch, "E32.top", {"start": v(1.5, 1) * mm, "end": v(0, 1) * mm});
            skLineSegment(sketch, "E32.left", {"start": v(1.5, 2) * mm, "end": v(1.5, 1) * mm});
            skLineSegment(sketch, "E32.right", {"start": v(0, 2) * mm, "end": v(0, 1) * mm});
            skSolve(sketch);
        }
        {
            var Q0;
            Q0 = qSketchRegion(id + "F25", true);
            extrude(context, id + "F26", {"entities" : qUnion([Q0]), "operationType" : NewBodyOperationType.REMOVE, "oppositeDirection" : true, "depth" : 2 * mm});
        }
        {
            var Q0;
            Q0=makeQuery(id+"F20.opExtrude","CAP_EDGE",EDGE,{"disambiguationData":[OSD([sQuery(id+"F18.wireOp",EDGE,"E26.MirrorCS")])],"isStart":false});
            chamfer(context, id + "F27", {"entities" : qUnion([Q0]), "width" : 0.8 * mm, "tangentPropagation" : true});
        }
        {
            var Q0;
            {var subQ0=sQuery(id+"F18.wireOp",EDGE,"E26.MirrorCS");Q0=makeQuery(id+"F27.opChamfer","BLEND_EDGE",EDGE,{"blendedFrom":[makeQuery(id+"F20.opExtrude","CAP_EDGE",EDGE,{"disambiguationData":[OSD([subQ0])],"isStart":false}),makeQuery(id+"F20.opExtrude","CAP_FACE",FACE,{"disambiguationData":[OSD([sQuery(id+"F18.wireOp",EDGE,"E25.MirrorCS"),subQ0,sQuery(id+"F18.wireOp",EDGE,"E27.MirrorCS"),sQuery(id+"F18.wireOp",EDGE,"E28.MirrorCS")])],"isStart":false})],"blendedInto":[makeQuery(id+"F20.opExtrude","CAP_FACE",FACE,{"disambiguationData":[OSD([sQuery(id+"F18.wireOp",EDGE,"E25.MirrorCS"),subQ0,sQuery(id+"F18.wireOp",EDGE,"E27.MirrorCS"),sQuery(id+"F18.wireOp",EDGE,"E28.MirrorCS")])],"isStart":false})]});}
            fillet(context, id + "F28", {"entities" : qUnion([Q0]), "radius" : 1 * mm, "tangentPropagation" : true, "allowEdgeOverflow" : false});
        }
    });
